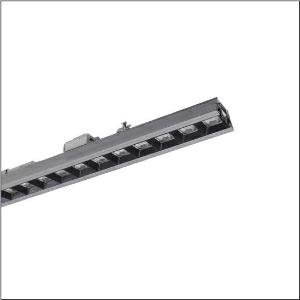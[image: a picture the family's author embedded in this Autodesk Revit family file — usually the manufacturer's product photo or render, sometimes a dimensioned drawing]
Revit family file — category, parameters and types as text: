
# Revit family: licross_21_silica_51ts12dn4zm00583xx
name_source: partatom
category: Lighting Fixtures
units: mm (PartAtom-declared; Revit-internal decimal feet)

## family parameters
Cut with Voids When Loaded = No
Host = Face
Light Source = No
Part Type = Normal
Room Calculation Point = No
Round Connector Dimension = Use Diameter
Shared = No

## types (1)
- --- (1 x LED, 6340 lm, 39 W, 4000K)
    Apparent Load = 39 VA
    CIE Flux Codes = 86 100 100 100 100
    Color Rendering = 80
    Color Temperature = 4000K
    Default Elevation = 1800 mm
    Description = Licross 21 Silica, luminaire insert, of sheet steel, galvanised, coil coated, silver, length: 1.500mm, width: 82mm, height: 86mm, LED rated luminous flux: 6.340lm, light colour: 840, SDCM (Standard Deviation of Colour Matching)MacAdam ≤ 3 SDCM (initial), control gear: DALI 2, with plug, 5-pole, with phase selection, mains connection: 220..240V, AC, 50/60Hz, rated input power: 39W, internal wiring halogen-free, primary light control with lens, of PMMA, primary anti-glare with darklight reflector, of PC, CAT 2 (L<= 1000cd/m²), light emission: direct distribution, primary light characteristic: symmetric, protection rating (complete): IP40, insulation class (complete): insulation class I (protective earthing), certification: CE, UKCA, protection symbol: D if used in an environment without relevant dust loads, impact resistance: IK03, permissible ambient temperature for indoor applications: -25..+45°C, corresponds to IFS (International Featured Standards) requirements for safety and quality in the food industry, reducing of maximum allowable ambient temperature of 5°C with ceiling mounting, LABS conformity tested according to VDMA 24364:2018-05, packaging unit: 1 piece
    Height = 86 mm
    Lamp = 1 x LED
    Lamp Light Flux = 6340 lm
    Lamp Power = 39 W
    Lamp count = 1
    Length = 1500 mm
    Luminous efficacy = 163 lm/W
    Manufacturer = Siteco
    ModVariant = No
    Model = 51TS12DN4ZM00583XX
    Mounting Place = Ceiling
    Mounting Type = Pendant
    Number of Poles = 1
    OnlyDefault = Yes
    Power Factor = 1
    Product Name = Licross 21 Silica
    Product group = luminaire insert | ceiling pendant
    ProductGroupID = 901
    Protection Class = Protection class I
    Protection Degree = IP 40
    RLX_Detail_Level = 1
    RLX_Emergency_Light_Flux = 0 lm
    RLX_Emergency_Type = 0
    RLX_Emergency_Type_DB = No
    RlxData = <blob elided: 57057 chars, md5=85970f5d>
    Socket = socket
    Standby Power = 0 W
    System Light Flux = 6340 lm
    System Power = 39 W
    Type Comments = factory setting: luminous flux: 100 % | dim-lin: 254 | 435 mA
    Type Image = l_1290833.jpg
    URL = http://relux.com
    VarID = @adj_107895
    Voltage = 0 V
    Weight = 0.00 kg
    Width = 82 mm  [stored 0.269029 ft]

note: [stored X ft] marks values corroborated as IEEE doubles in the binary element streams (Revit-internal decimal feet)

## geometry (parser evidence)
native form markers: Blend x4, Sweep x12
no freeform markers — native parametric forms only
